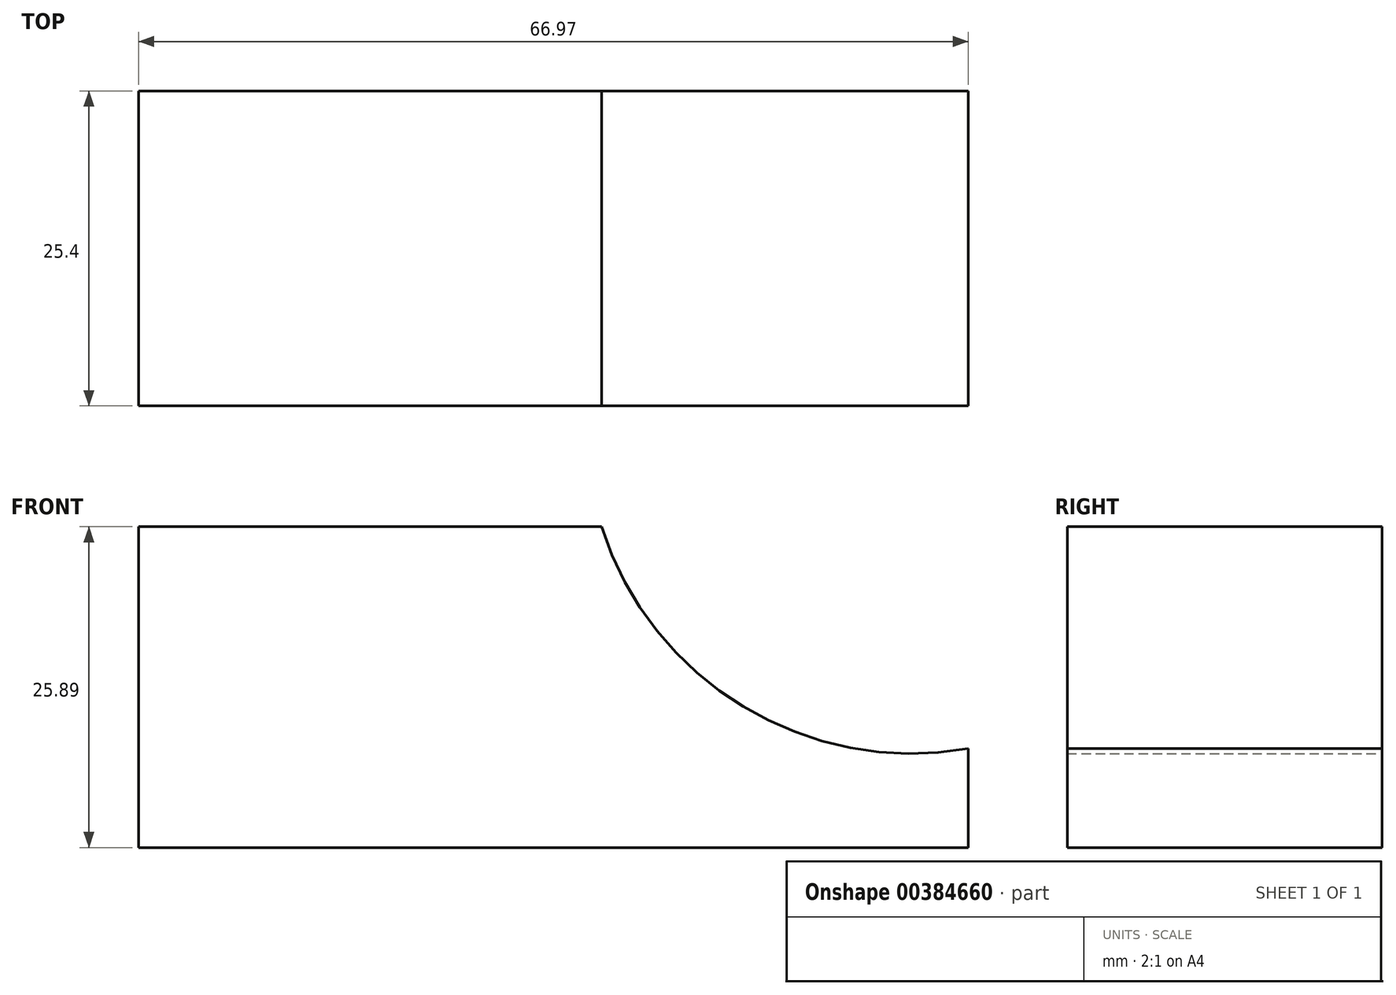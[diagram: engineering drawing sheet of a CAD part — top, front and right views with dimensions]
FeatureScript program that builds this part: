
annotation { "Feature Type Name" : "Feature", "Feature Type Description" : "" }
export const myFeature = defineFeature(function(context is Context, id is Id, definition is map)
    precondition{}
    {
        {
            var Q0;
            Q0=qCreatedBy(makeId("Front.planeOp"),FACE);
            var sketch = newSketch(context, id + "F0", { "sketchPlane" : qUnion([Q0])});
            skLineSegment(sketch, "E0", {"start": v(0, 0) * mm, "end": v(66.97, 0) * mm});
            skLineSegment(sketch, "E1", {"start": v(0, 0) * mm, "end": v(0, 25.9) * mm});
            skLineSegment(sketch, "E2", {"start": v(0, 25.9) * mm, "end": v(37.38, 25.9) * mm});
            skLineSegment(sketch, "E3", {"start": v(66.97, 0) * mm, "end": v(66.97, 7.98) * mm});
            skArc(sketch, "E4", {"start": v(37.38, 25.9) * mm, "mid": v(48.8, 11.38) * mm, "end": v(66.97, 7.98) * mm});
            skSolve(sketch);
        }
        {
            var Q0;
            Q0 = qSketchRegion(id + "F0", true);
            extrude(context, id + "F1", {"entities" : qUnion([Q0]), "depth" : 25.4 * mm});
        }
    });
